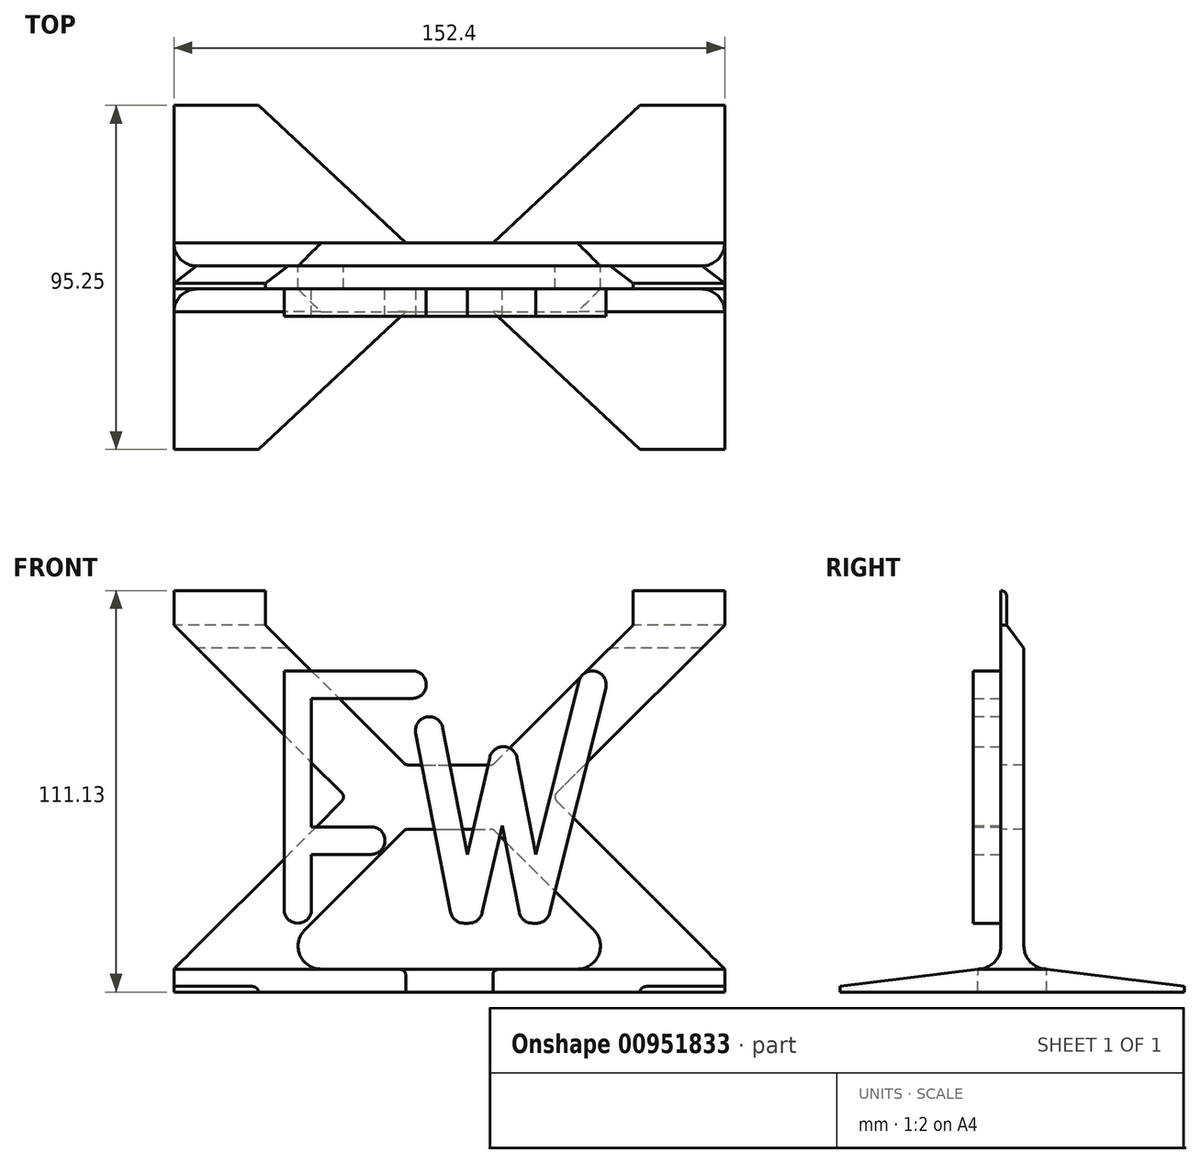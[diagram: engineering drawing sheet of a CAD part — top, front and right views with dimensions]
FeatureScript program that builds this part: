
annotation { "Feature Type Name" : "Feature", "Feature Type Description" : "" }
export const myFeature = defineFeature(function(context is Context, id is Id, definition is map)
    precondition{}
    {
        {
            var Q0;
            Q0=qCreatedBy(makeId("Right.planeOp"),FACE);
            var sketch = newSketch(context, id + "F0", { "sketchPlane" : qUnion([Q0])});
            skLineSegment(sketch, "E0", {"start": v(0, 9.53) * mm, "end": v(1.59, 9.53) * mm});
            skLineSegment(sketch, "E1", {"start": v(1.59, 9.53) * mm, "end": v(1.59, 0) * mm});
            skLineSegment(sketch, "E2", {"start": v(1.59, 0) * mm, "end": v(6.35, -6.35) * mm});
            skLineSegment(sketch, "E3", {"start": v(6.35, -6.35) * mm, "end": v(6.35, -95.25) * mm});
            skLineSegment(sketch, "E4", {"start": v(6.35, -95.25) * mm, "end": v(50.8, -95.25) * mm});
            skLineSegment(sketch, "E5", {"start": v(50.8, -95.25) * mm, "end": v(50.8, -101.6) * mm});
            skLineSegment(sketch, "E6", {"start": v(0, 9.53) * mm, "end": v(0, -95.25) * mm});
            skLineSegment(sketch, "E7", {"start": v(-44.45, -101.6) * mm, "end": v(-44.45, -95.25) * mm});
            skLineSegment(sketch, "E8", {"start": v(-44.45, -95.25) * mm, "end": v(0, -95.25) * mm});
            skLineSegment(sketch, "E9", {"start": v(-44.45, -101.6) * mm, "end": v(50.8, -101.6) * mm});
            skSolve(sketch);
        }
        {
            var Q0;
            Q0 = qSketchRegion(id + "F0", true);
            extrude(context, id + "F1", {"entities" : qUnion([Q0]), "endBound" : BoundingType.SYMMETRIC, "depth" : 152.4 * mm, "offsetDistance" : 25.4 * mm});
        }
        {
            var Q0;
            Q0=makeQuery(id+"F1.opExtrude","SWEPT_FACE",FACE,{"disambiguationData":[OSD([sQuery(id+"F0.wireOp",EDGE,"E8")])]});
            var sketch = newSketch(context, id + "F2", { "sketchPlane" : qUnion([Q0])});
            skLineSegment(sketch, "E10", {"start": v(63.5, 0) * mm, "end": v(63.5, -44.45) * mm});
            skLineSegment(sketch, "E11", {"start": v(0, -44.45) * mm, "end": v(0, 0) * mm});
            skLineSegment(sketch, "E12", {"start": v(-63.5, -44.45) * mm, "end": v(-63.5, 0) * mm});
            skLineSegment(sketch, "E13", {"start": v(-36.08, 3.18) * mm, "end": v(33.95, 3.18) * mm, "construction": true});
            skLineSegment(sketch, "E14.MirrorCS", {"start": v(-63.5, 50.8) * mm, "end": v(-63.5, 6.35) * mm});
            skLineSegment(sketch, "E15.MirrorCS", {"start": v(0, 50.8) * mm, "end": v(0, 6.35) * mm});
            skLineSegment(sketch, "E16.MirrorCS", {"start": v(63.5, 6.35) * mm, "end": v(63.5, 50.8) * mm});
            skSolve(sketch);
        }
        {
            var Q0;
            Q0=makeQuery(id+"F1.opExtrude","SWEPT_FACE",FACE,{"disambiguationData":[OSD([sQuery(id+"F0.wireOp",EDGE,"E6")])]});
            var sketch = newSketch(context, id + "F3", { "sketchPlane" : qUnion([Q0])});
            skLineSegment(sketch, "E17", {"start": v(-45.72, -12.7) * mm, "end": v(-45.72, -82.55) * mm});
            skLineSegment(sketch, "E18", {"start": v(-45.72, -82.55) * mm, "end": v(-38.1, -82.55) * mm});
            skLineSegment(sketch, "E19", {"start": v(-38.1, -82.55) * mm, "end": v(-38.1, -63.5) * mm});
            skLineSegment(sketch, "E20", {"start": v(-38.1, -63.5) * mm, "end": v(-17.78, -63.5) * mm});
            skLineSegment(sketch, "E21", {"start": v(-17.78, -63.5) * mm, "end": v(-17.78, -55.88) * mm});
            skLineSegment(sketch, "E22", {"start": v(-17.78, -55.88) * mm, "end": v(-38.1, -55.88) * mm});
            skLineSegment(sketch, "E23", {"start": v(-38.1, -55.88) * mm, "end": v(-38.1, -20.32) * mm});
            skLineSegment(sketch, "E24", {"start": v(-38.1, -20.32) * mm, "end": v(-6.35, -20.32) * mm});
            skLineSegment(sketch, "E25", {"start": v(-6.35, -20.32) * mm, "end": v(-6.35, -12.7) * mm});
            skLineSegment(sketch, "E26", {"start": v(-6.35, -12.7) * mm, "end": v(-45.72, -12.7) * mm});
            skLineSegment(sketch, "E27", {"start": v(-10.16, -25.4) * mm, "end": v(0.95, -82.55) * mm});
            skLineSegment(sketch, "E28", {"start": v(27.07, -82.55) * mm, "end": v(44.49, -12.7) * mm});
            skLineSegment(sketch, "E29", {"start": v(44.49, -12.7) * mm, "end": v(36.64, -12.7) * mm});
            skLineSegment(sketch, "E30", {"start": v(36.64, -12.7) * mm, "end": v(23.97, -63.5) * mm});
            skLineSegment(sketch, "E31", {"start": v(5, -63.5) * mm, "end": v(-2.4, -25.4) * mm});
            skLineSegment(sketch, "E32", {"start": v(-86.99, 0) * mm, "end": v(146.26, 0) * mm, "construction": true});
            skLineSegment(sketch, "E33", {"start": v(5, -63.5) * mm, "end": v(11.2, -36.7) * mm});
            skLineSegment(sketch, "E34", {"start": v(18.79, -36.83) * mm, "end": v(23.97, -63.5) * mm});
            skLineSegment(sketch, "E35", {"start": v(-10.16, -25.4) * mm, "end": v(-2.4, -25.4) * mm});
            skLineSegment(sketch, "E36", {"start": v(0.95, -82.55) * mm, "end": v(8.43, -82.55) * mm});
            skLineSegment(sketch, "E37", {"start": v(8.43, -82.55) * mm, "end": v(14.66, -55.56) * mm});
            skLineSegment(sketch, "E38", {"start": v(14.66, -55.56) * mm, "end": v(19.91, -82.55) * mm});
            skLineSegment(sketch, "E39", {"start": v(19.91, -82.55) * mm, "end": v(27.07, -82.55) * mm});
            skLineSegment(sketch, "E40", {"start": v(5, -63.5) * mm, "end": v(5, -15.04) * mm, "construction": true});
            skArc(sketch, "E41", {"start": v(18.79, -36.83) * mm, "mid": v(15.04, -33.7) * mm, "end": v(11.2, -36.7) * mm});
            skSolve(sketch);
        }
        {
            var Q0;
            Q0 = qSketchRegion(id + "F3", true);
            extrude(context, id + "F4", {"entities" : qUnion([Q0]), "depth" : 7.62 * mm, "offsetDistance" : 25.4 * mm});
        }
        {
            var Q0;
            Q0=makeQuery(id+"F4.opExtrude","SWEPT_EDGE",EDGE,{"disambiguationData":[OSD([sQuery(id+"F3.wireOp",EDGE,"E27"),sQuery(id+"F3.wireOp",EDGE,"E35")])]});
            var Q1;
            Q1=makeQuery(id+"F4.opExtrude","SWEPT_EDGE",EDGE,{"disambiguationData":[OSD([sQuery(id+"F3.wireOp",EDGE,"E31"),sQuery(id+"F3.wireOp",EDGE,"E35")])]});
            var Q2;
            Q2=makeQuery(id+"F4.opExtrude","SWEPT_EDGE",EDGE,{"disambiguationData":[OSD([sQuery(id+"F3.wireOp",EDGE,"E29"),sQuery(id+"F3.wireOp",EDGE,"E30")])]});
            var Q3;
            Q3=makeQuery(id+"F4.opExtrude","SWEPT_EDGE",EDGE,{"disambiguationData":[OSD([sQuery(id+"F3.wireOp",EDGE,"E28"),sQuery(id+"F3.wireOp",EDGE,"E29")])]});
            var Q4;
            Q4=makeQuery(id+"F4.opExtrude","SWEPT_EDGE",EDGE,{"disambiguationData":[OSD([sQuery(id+"F3.wireOp",EDGE,"E28"),sQuery(id+"F3.wireOp",EDGE,"E39")])]});
            var Q5;
            Q5=makeQuery(id+"F4.opExtrude","SWEPT_EDGE",EDGE,{"disambiguationData":[OSD([sQuery(id+"F3.wireOp",EDGE,"E36"),sQuery(id+"F3.wireOp",EDGE,"E37")])]});
            var Q6;
            Q6=makeQuery(id+"F4.opExtrude","SWEPT_EDGE",EDGE,{"disambiguationData":[OSD([sQuery(id+"F3.wireOp",EDGE,"E38"),sQuery(id+"F3.wireOp",EDGE,"E39")])]});
            var Q7;
            Q7=makeQuery(id+"F4.opExtrude","SWEPT_EDGE",EDGE,{"disambiguationData":[OSD([sQuery(id+"F3.wireOp",EDGE,"E27"),sQuery(id+"F3.wireOp",EDGE,"E36")])]});
            var Q8;
            Q8=makeQuery(id+"F4.opExtrude","SWEPT_EDGE",EDGE,{"disambiguationData":[OSD([sQuery(id+"F3.wireOp",EDGE,"E20"),sQuery(id+"F3.wireOp",EDGE,"E21")])]});
            var Q9;
            Q9=makeQuery(id+"F4.opExtrude","SWEPT_EDGE",EDGE,{"disambiguationData":[OSD([sQuery(id+"F3.wireOp",EDGE,"E21"),sQuery(id+"F3.wireOp",EDGE,"E22")])]});
            var Q10;
            Q10=makeQuery(id+"F4.opExtrude","SWEPT_EDGE",EDGE,{"disambiguationData":[OSD([sQuery(id+"F3.wireOp",EDGE,"E24"),sQuery(id+"F3.wireOp",EDGE,"E25")])]});
            var Q11;
            Q11=makeQuery(id+"F4.opExtrude","SWEPT_EDGE",EDGE,{"disambiguationData":[OSD([sQuery(id+"F3.wireOp",EDGE,"E18"),sQuery(id+"F3.wireOp",EDGE,"E19")])]});
            var Q12;
            Q12=makeQuery(id+"F4.opExtrude","SWEPT_EDGE",EDGE,{"disambiguationData":[OSD([sQuery(id+"F3.wireOp",EDGE,"E25"),sQuery(id+"F3.wireOp",EDGE,"E26")])]});
            var Q13;
            Q13=makeQuery(id+"F4.opExtrude","SWEPT_EDGE",EDGE,{"disambiguationData":[OSD([sQuery(id+"F3.wireOp",EDGE,"E17"),sQuery(id+"F3.wireOp",EDGE,"E18")])]});
            fillet(context, id + "F5", {"entities" : qUnion([Q0, Q1, Q2, Q3, Q4, Q5, Q6, Q7, Q8, Q9, Q10, Q11, Q12, Q13]), "radius" : 3.8 * mm, "tangentPropagation" : true, "allowEdgeOverflow" : false});
        }
        {
            var Q0;
            Q0=makeQuery(id+"F1.opExtrude","SWEPT_FACE",FACE,{"disambiguationData":[OSD([sQuery(id+"F0.wireOp",EDGE,"E6")])]});
            var sketch = newSketch(context, id + "F6", { "sketchPlane" : qUnion([Q0])});
            skLineSegment(sketch, "E42", {"start": v(-76.2, 0) * mm, "end": v(-28.57, -47.63) * mm});
            skLineSegment(sketch, "E43", {"start": v(-28.58, -47.63) * mm, "end": v(-76.2, -95.25) * mm});
            skLineSegment(sketch, "E44", {"start": v(-76.2, -95.25) * mm, "end": v(-76.2, 0) * mm});
            skLineSegment(sketch, "E45", {"start": v(76.2, 0) * mm, "end": v(28.57, -47.63) * mm});
            skLineSegment(sketch, "E46", {"start": v(28.57, -47.63) * mm, "end": v(76.2, -95.25) * mm});
            skLineSegment(sketch, "E47", {"start": v(76.2, -95.25) * mm, "end": v(76.2, 0) * mm});
            skLineSegment(sketch, "E48", {"start": v(-28.58, -47.63) * mm, "end": v(-76.2, -47.63) * mm, "construction": true});
            skLineSegment(sketch, "E49", {"start": v(28.58, -47.63) * mm, "end": v(76.2, -47.63) * mm, "construction": true});
            skLineSegment(sketch, "E50", {"start": v(-50.8, -95.25) * mm, "end": v(-12.06, -56.51) * mm});
            skLineSegment(sketch, "E51", {"start": v(12.06, -56.51) * mm, "end": v(50.8, -95.25) * mm});
            skLineSegment(sketch, "E52", {"start": v(-12.06, -56.52) * mm, "end": v(12.06, -56.52) * mm});
            skLineSegment(sketch, "E53.MirrorCS", {"start": v(-12.06, -38.74) * mm, "end": v(12.06, -38.74) * mm});
            skLineSegment(sketch, "E54.MirrorCS", {"start": v(-50.8, 0) * mm, "end": v(-12.06, -38.74) * mm});
            skLineSegment(sketch, "E55.MirrorCS", {"start": v(12.06, -38.74) * mm, "end": v(50.8, 0) * mm});
            skLineSegment(sketch, "E56", {"start": v(-50.8, 0) * mm, "end": v(-50.8, 9.53) * mm});
            skLineSegment(sketch, "E57", {"start": v(50.8, 0) * mm, "end": v(50.8, 9.53) * mm});
            skLineSegment(sketch, "E58", {"start": v(50.8, 9.53) * mm, "end": v(-50.8, 9.53) * mm});
            skSolve(sketch);
        }
        {
            var Q0;
            Q0=makeQuery(id+"F6.imprint","IMPRINT",FACE,{"disambiguationData":[TD([[makeQuery(id+"F6.imprint","IMPRINT",EDGE,{"derivedFrom":sQuery(id+"F6.wireOp",EDGE,"E45")}),1.0]])]});
            var Q1;
            Q1=makeQuery(id+"F6.imprint","IMPRINT",FACE,{"disambiguationData":[TD([[makeQuery(id+"F6.imprint","IMPRINT",EDGE,{"derivedFrom":sQuery(id+"F6.wireOp",EDGE,"E53.MirrorCS")}),1.0]])]});
            var Q2;
            {var subQ0=sQuery(id+"F6.wireOp",EDGE,"E50");Q2=makeQuery(id+"F6.imprint","IMPRINT",FACE,{"disambiguationData":[TD([[makeQuery(id+"F6.imprint","IMPRINT",EDGE,{"derivedFrom":subQ0}),-1.0]])]});}
            var Q3;
            Q3=makeQuery(id+"F6.imprint","IMPRINT",FACE,{"disambiguationData":[TD([[makeQuery(id+"F6.imprint","IMPRINT",EDGE,{"derivedFrom":sQuery(id+"F6.wireOp",EDGE,"E42")}),-1.0]])]});
            var Q4;
            Q4=makeQuery(id+"F6.imprint","IMPRINT",FACE,{"disambiguationData":[TD([[makeQuery(id+"F6.imprint","IMPRINT",EDGE,{"derivedFrom":sQuery(id+"F6.wireOp",EDGE,"6XojoKTg-mtFg-S1lx-smN3-pDs7Ketdyg1A")}),1.0]])]});
            extrude(context, id + "F7", {"entities" : qUnion([Q0, Q1, Q2, Q3, Q4]), "operationType" : NewBodyOperationType.REMOVE, "endBound" : BoundingType.UP_TO_NEXT, "oppositeDirection" : true, "depth" : 25.4 * mm, "offsetDistance" : 25.4 * mm});
        }
        {
            var Q0;
            {var subQ0=sQuery(id+"F0.wireOp",EDGE,"E8");var subQ1=sQuery(id+"F0.wireOp",EDGE,"E6");Q0=makeQuery(id+"F7.boolean.opBoolean","SPLIT",EDGE,{"disambiguationData":[TD([makeQuery(id+"F7.opExtrude","SWEPT_FACE",FACE,{"disambiguationData":[OSD([sQuery(id+"F6.wireOp",EDGE,"E43")])]})])],"derivedFrom":makeQuery(id+"F1.opExtrude","SWEPT_EDGE",EDGE,{"disambiguationData":[OSD([subQ1,subQ0])]})});}
            var Q1;
            {var subQ0=sQuery(id+"F0.wireOp",EDGE,"E8");var subQ1=sQuery(id+"F0.wireOp",EDGE,"E6");Q1=makeQuery(id+"F7.boolean.opBoolean","SPLIT",EDGE,{"disambiguationData":[TD([makeQuery(id+"F7.opExtrude","SWEPT_FACE",FACE,{"disambiguationData":[OSD([sQuery(id+"F6.wireOp",EDGE,"E46")])]})])],"derivedFrom":makeQuery(id+"F1.opExtrude","SWEPT_EDGE",EDGE,{"disambiguationData":[OSD([subQ1,subQ0])]})});}
            var Q2;
            {var subQ0=sQuery(id+"F0.wireOp",EDGE,"E4");var subQ2=sQuery(id+"F0.wireOp",EDGE,"E3");Q2=makeQuery(id+"F7.boolean.opBoolean","SPLIT",EDGE,{"disambiguationData":[TD([makeQuery(id+"F7.opExtrude","SWEPT_FACE",FACE,{"disambiguationData":[OSD([sQuery(id+"F6.wireOp",EDGE,"E46")])]})])],"derivedFrom":makeQuery(id+"F1.opExtrude","SWEPT_EDGE",EDGE,{"disambiguationData":[OSD([subQ2,subQ0])]})});}
            var Q3;
            {var subQ1=sQuery(id+"F0.wireOp",EDGE,"E3");var subQ2=sQuery(id+"F0.wireOp",EDGE,"E4");Q3=makeQuery(id+"F7.boolean.opBoolean","SPLIT",EDGE,{"disambiguationData":[TD([makeQuery(id+"F7.opExtrude","SWEPT_FACE",FACE,{"disambiguationData":[OSD([sQuery(id+"F6.wireOp",EDGE,"E43")])]})])],"derivedFrom":makeQuery(id+"F1.opExtrude","SWEPT_EDGE",EDGE,{"disambiguationData":[OSD([subQ1,subQ2])]})});}
            var Q4;
            Q4=makeQuery(id+"F7.boolean.opBoolean","COPY",EDGE,{"derivedFrom":makeQuery(id+"F7.opExtrude","SWEPT_EDGE",EDGE,{"disambiguationData":[OSD([sQuery(id+"F0.wireOp",EDGE,"E6"),sQuery(id+"F0.wireOp",EDGE,"E8"),sQuery(id+"F6.wireOp",EDGE,"E50")])]})});
            var Q5;
            Q5=makeQuery(id+"F7.boolean.opBoolean","COPY",EDGE,{"derivedFrom":makeQuery(id+"F7.opExtrude","SWEPT_EDGE",EDGE,{"disambiguationData":[OSD([sQuery(id+"F0.wireOp",EDGE,"E6"),sQuery(id+"F0.wireOp",EDGE,"E8"),sQuery(id+"F6.wireOp",EDGE,"E51")])]})});
            fillet(context, id + "F8", {"entities" : qUnion([Q0, Q1, Q2, Q3, Q4, Q5]), "radius" : 6.35 * mm, "tangentPropagation" : true, "allowEdgeOverflow" : false});
        }
        {
            var Q0;
            {var subQ0=sQuery(id+"F0.wireOp",EDGE,"E6");var subQ1=sQuery(id+"F0.wireOp",EDGE,"E5");var subQ2=sQuery(id+"F0.wireOp",EDGE,"E4");var subQ3=sQuery(id+"F0.wireOp",EDGE,"E3");var subQ4=sQuery(id+"F0.wireOp",EDGE,"E7");var subQ5=sQuery(id+"F0.wireOp",EDGE,"E8");var subQ6=sQuery(id+"F0.wireOp",EDGE,"E9");Q0=makeQuery(id+"F7.boolean.opBoolean","SPLIT",FACE,{"disambiguationData":[TD([makeQuery(id+"F1.opExtrude","SWEPT_FACE",FACE,{"disambiguationData":[OSD([subQ3])]})])],"derivedFrom":makeQuery(id+"F1.opExtrude","CAP_FACE",FACE,{"disambiguationData":[OSD([sQuery(id+"F0.wireOp",EDGE,"E0"),sQuery(id+"F0.wireOp",EDGE,"E1"),sQuery(id+"F0.wireOp",EDGE,"E2"),subQ3,subQ2,subQ1,subQ0,subQ4,subQ5,subQ6])],"isStart":false})});}
            var sketch = newSketch(context, id + "F9", { "sketchPlane" : qUnion([Q0])});
            skLineSegment(sketch, "E59", {"start": v(-6.35, -95.25) * mm, "end": v(-44.45, -100.01) * mm});
            skLineSegment(sketch, "E60", {"start": v(-44.45, -100.01) * mm, "end": v(-44.45, -95.25) * mm});
            skLineSegment(sketch, "E61", {"start": v(-44.45, -95.25) * mm, "end": v(-6.35, -95.25) * mm});
            skLineSegment(sketch, "E62", {"start": v(3.18, -95.25) * mm, "end": v(3.18, -76.25) * mm, "construction": true});
            skLineSegment(sketch, "E63.MirrorCS", {"start": v(12.7, -95.25) * mm, "end": v(50.8, -100.01) * mm});
            skLineSegment(sketch, "E64.MirrorCS", {"start": v(50.8, -95.25) * mm, "end": v(12.7, -95.25) * mm});
            skLineSegment(sketch, "E65.MirrorCS", {"start": v(50.8, -100.01) * mm, "end": v(50.8, -95.25) * mm});
            skSolve(sketch);
        }
        {
            var Q0;
            Q0 = qSketchRegion(id + "F9", true);
            extrude(context, id + "F10", {"entities" : qUnion([Q0]), "operationType" : NewBodyOperationType.REMOVE, "endBound" : BoundingType.THROUGH_ALL, "oppositeDirection" : true, "depth" : 25.4 * mm, "offsetDistance" : 25.4 * mm});
        }
        {
            var Q0;
            {var subQ0=sQuery(id+"F0.wireOp",EDGE,"E8");Q0=makeQuery(id+"F7.boolean.opBoolean","MERGE",FACE,{"derivedFrom":[makeQuery(id+"F1.opExtrude","SWEPT_FACE",FACE,{"disambiguationData":[OSD([sQuery(id+"F0.wireOp",EDGE,"E4")])]}),makeQuery(id+"F1.opExtrude","SWEPT_FACE",FACE,{"disambiguationData":[OSD([subQ0])]})],"fromTools":[makeQuery(id+"F7.opExtrude","SWEPT_FACE",FACE,{"disambiguationData":[OSD([sQuery(id+"F0.wireOp",EDGE,"E6"),subQ0])]})]});}
            var sketch = newSketch(context, id + "F11", { "sketchPlane" : qUnion([Q0])});
            skLineSegment(sketch, "E66", {"start": v(52.8, 50.8) * mm, "end": v(12.06, 12.7) * mm});
            skLineSegment(sketch, "E67", {"start": v(12.06, 12.7) * mm, "end": v(-12.06, 12.7) * mm});
            skLineSegment(sketch, "E68", {"start": v(-12.06, 12.7) * mm, "end": v(-52.8, 50.8) * mm});
            skLineSegment(sketch, "E69", {"start": v(-52.8, 50.8) * mm, "end": v(52.8, 50.8) * mm});
            skLineSegment(sketch, "E70.MirrorCS", {"start": v(52.8, -44.45) * mm, "end": v(12.06, -6.35) * mm});
            skLineSegment(sketch, "E71.MirrorCS", {"start": v(-52.8, -44.45) * mm, "end": v(52.8, -44.45) * mm});
            skLineSegment(sketch, "E72.MirrorCS", {"start": v(-12.06, -6.35) * mm, "end": v(-52.8, -44.45) * mm});
            skLineSegment(sketch, "E73.MirrorCS", {"start": v(12.06, -6.35) * mm, "end": v(-12.06, -6.35) * mm});
            skLineSegment(sketch, "E74", {"start": v(76.2, 50.8) * mm, "end": v(35.47, 12.7) * mm});
            skLineSegment(sketch, "E75", {"start": v(35.47, 12.7) * mm, "end": v(76.2, 12.7) * mm});
            skLineSegment(sketch, "E76", {"start": v(76.2, 12.7) * mm, "end": v(76.2, 50.8) * mm});
            skLineSegment(sketch, "E77.MirrorCS", {"start": v(-76.2, 50.8) * mm, "end": v(-35.47, 12.7) * mm});
            skLineSegment(sketch, "E78.MirrorCS", {"start": v(-35.47, 12.7) * mm, "end": v(-76.2, 12.7) * mm});
            skLineSegment(sketch, "E79.MirrorCS", {"start": v(-76.2, 12.7) * mm, "end": v(-76.2, 50.8) * mm});
            skLineSegment(sketch, "E80.MirrorCS", {"start": v(-35.47, -6.35) * mm, "end": v(-76.2, -6.35) * mm});
            skLineSegment(sketch, "E81.MirrorCS", {"start": v(-76.2, -44.45) * mm, "end": v(-35.47, -6.35) * mm});
            skLineSegment(sketch, "E82.MirrorCS", {"start": v(-76.2, -6.35) * mm, "end": v(-76.2, -44.45) * mm});
            skLineSegment(sketch, "E83.MirrorCS", {"start": v(76.2, -44.45) * mm, "end": v(35.47, -6.35) * mm});
            skLineSegment(sketch, "E84.MirrorCS", {"start": v(76.2, -6.35) * mm, "end": v(76.2, -44.45) * mm});
            skLineSegment(sketch, "E85.MirrorCS", {"start": v(35.47, -6.35) * mm, "end": v(76.2, -6.35) * mm});
            skSolve(sketch);
        }
        {
            var Q0;
            Q0=makeQuery(id+"F11.imprint","IMPRINT",FACE,{"disambiguationData":[TD([[makeQuery(id+"F11.imprint","IMPRINT",EDGE,{"derivedFrom":sQuery(id+"F11.wireOp",EDGE,"E70.MirrorCS")}),1.0]])]});
            var Q1;
            Q1=makeQuery(id+"F11.imprint","IMPRINT",FACE,{"disambiguationData":[TD([[makeQuery(id+"F11.imprint","IMPRINT",EDGE,{"derivedFrom":sQuery(id+"F11.wireOp",EDGE,"E66")}),-1.0]])]});
            extrude(context, id + "F12", {"entities" : qUnion([Q0, Q1]), "operationType" : NewBodyOperationType.REMOVE, "endBound" : BoundingType.THROUGH_ALL, "oppositeDirection" : true, "depth" : 25.4 * mm, "offsetDistance" : 25.4 * mm});
        }
        {
            var Q0;
            {var subQ0=sQuery(id+"F0.wireOp",EDGE,"E7");var subQ1=sQuery(id+"F9.wireOp",EDGE,"E59");Q0=makeQuery(id+"F12.boolean.opBoolean","SPLIT",EDGE,{"disambiguationData":[TD([makeQuery(id+"F12.opExtrude","SWEPT_FACE",FACE,{"disambiguationData":[OSD([sQuery(id+"F11.wireOp",EDGE,"E70.MirrorCS")])]})])],"derivedFrom":makeQuery(id+"F10.boolean.opBoolean","COPY",EDGE,{"derivedFrom":makeQuery(id+"F10.opExtrude","SWEPT_EDGE",EDGE,{"disambiguationData":[OSD([subQ0,subQ1,sQuery(id+"F9.wireOp",EDGE,"E60")])]})})});}
            var Q1;
            {var subQ0=sQuery(id+"F0.wireOp",EDGE,"E7");var subQ1=sQuery(id+"F9.wireOp",EDGE,"E59");Q1=makeQuery(id+"F12.boolean.opBoolean","SPLIT",EDGE,{"disambiguationData":[TD([makeQuery(id+"F12.opExtrude","SWEPT_FACE",FACE,{"disambiguationData":[OSD([sQuery(id+"F11.wireOp",EDGE,"E72.MirrorCS")])]})])],"derivedFrom":makeQuery(id+"F10.boolean.opBoolean","COPY",EDGE,{"derivedFrom":makeQuery(id+"F10.opExtrude","SWEPT_EDGE",EDGE,{"disambiguationData":[OSD([subQ0,subQ1,sQuery(id+"F9.wireOp",EDGE,"E60")])]})})});}
            var Q2;
            Q2=makeQuery(id+"F12.boolean.opBoolean","INTERSECT",EDGE,{"derivedFrom":[makeQuery(id+"F10.boolean.opBoolean","COPY",FACE,{"derivedFrom":makeQuery(id+"F10.opExtrude","SWEPT_FACE",FACE,{"disambiguationData":[OSD([sQuery(id+"F9.wireOp",EDGE,"E59")])]})}),makeQuery(id+"F12.opExtrude","SWEPT_FACE",FACE,{"disambiguationData":[OSD([sQuery(id+"F11.wireOp",EDGE,"E72.MirrorCS")])]})]});
            var Q3;
            Q3=makeQuery(id+"F12.boolean.opBoolean","INTERSECT",EDGE,{"derivedFrom":[makeQuery(id+"F10.boolean.opBoolean","COPY",FACE,{"derivedFrom":makeQuery(id+"F10.opExtrude","SWEPT_FACE",FACE,{"disambiguationData":[OSD([sQuery(id+"F9.wireOp",EDGE,"E59")])]})}),makeQuery(id+"F12.opExtrude","SWEPT_FACE",FACE,{"disambiguationData":[OSD([sQuery(id+"F11.wireOp",EDGE,"E70.MirrorCS")])]})]});
            var Q4;
            {var subQ0=sQuery(id+"F0.wireOp",EDGE,"E5");var subQ1=sQuery(id+"F9.wireOp",EDGE,"E63.MirrorCS");Q4=makeQuery(id+"F12.boolean.opBoolean","SPLIT",EDGE,{"disambiguationData":[TD([makeQuery(id+"F12.opExtrude","SWEPT_FACE",FACE,{"disambiguationData":[OSD([sQuery(id+"F11.wireOp",EDGE,"E66")])]})])],"derivedFrom":makeQuery(id+"F10.boolean.opBoolean","COPY",EDGE,{"derivedFrom":makeQuery(id+"F10.opExtrude","SWEPT_EDGE",EDGE,{"disambiguationData":[OSD([subQ0,subQ1,sQuery(id+"F9.wireOp",EDGE,"E65.MirrorCS")])]})})});}
            var Q5;
            Q5=makeQuery(id+"F12.boolean.opBoolean","INTERSECT",EDGE,{"derivedFrom":[makeQuery(id+"F10.boolean.opBoolean","COPY",FACE,{"derivedFrom":makeQuery(id+"F10.opExtrude","SWEPT_FACE",FACE,{"disambiguationData":[OSD([sQuery(id+"F9.wireOp",EDGE,"E63.MirrorCS")])]})}),makeQuery(id+"F12.opExtrude","SWEPT_FACE",FACE,{"disambiguationData":[OSD([sQuery(id+"F11.wireOp",EDGE,"E66")])]})]});
            var Q6;
            Q6=makeQuery(id+"F12.boolean.opBoolean","INTERSECT",EDGE,{"derivedFrom":[makeQuery(id+"F10.boolean.opBoolean","COPY",FACE,{"derivedFrom":makeQuery(id+"F10.opExtrude","SWEPT_FACE",FACE,{"disambiguationData":[OSD([sQuery(id+"F9.wireOp",EDGE,"E63.MirrorCS")])]})}),makeQuery(id+"F12.opExtrude","SWEPT_FACE",FACE,{"disambiguationData":[OSD([sQuery(id+"F11.wireOp",EDGE,"E68")])]})]});
            var Q7;
            {var subQ0=sQuery(id+"F0.wireOp",EDGE,"E5");var subQ1=sQuery(id+"F9.wireOp",EDGE,"E63.MirrorCS");Q7=makeQuery(id+"F12.boolean.opBoolean","SPLIT",EDGE,{"disambiguationData":[TD([makeQuery(id+"F12.opExtrude","SWEPT_FACE",FACE,{"disambiguationData":[OSD([sQuery(id+"F11.wireOp",EDGE,"E68")])]})])],"derivedFrom":makeQuery(id+"F10.boolean.opBoolean","COPY",EDGE,{"derivedFrom":makeQuery(id+"F10.opExtrude","SWEPT_EDGE",EDGE,{"disambiguationData":[OSD([subQ0,subQ1,sQuery(id+"F9.wireOp",EDGE,"E65.MirrorCS")])]})})});}
            var Q8;
            {var subQ0=sQuery(id+"F0.wireOp",EDGE,"E0");var subQ1=sQuery(id+"F0.wireOp",EDGE,"E1");Q8=makeQuery(id+"F7.boolean.opBoolean","SPLIT",EDGE,{"disambiguationData":[TD([makeQuery(id+"F7.opExtrude","SWEPT_FACE",FACE,{"disambiguationData":[OSD([sQuery(id+"F6.wireOp",EDGE,"E56")])]})])],"derivedFrom":makeQuery(id+"F1.opExtrude","SWEPT_EDGE",EDGE,{"disambiguationData":[OSD([subQ0,subQ1])]})});}
            var Q9;
            {var subQ0=sQuery(id+"F0.wireOp",EDGE,"E0");var subQ1=sQuery(id+"F0.wireOp",EDGE,"E1");Q9=makeQuery(id+"F7.boolean.opBoolean","SPLIT",EDGE,{"disambiguationData":[TD([makeQuery(id+"F7.opExtrude","SWEPT_FACE",FACE,{"disambiguationData":[OSD([sQuery(id+"F6.wireOp",EDGE,"E57")])]})])],"derivedFrom":makeQuery(id+"F1.opExtrude","SWEPT_EDGE",EDGE,{"disambiguationData":[OSD([subQ0,subQ1])]})});}
            var Q10;
            Q10=makeQuery(id+"F7.boolean.opBoolean","COPY",EDGE,{"derivedFrom":makeQuery(id+"F7.opExtrude","CAP_EDGE",EDGE,{"disambiguationData":[OSD([sQuery(id+"F6.wireOp",EDGE,"E46")])],"isStart":true})});
            var Q11;
            Q11=makeQuery(id+"F7.boolean.opBoolean","COPY",EDGE,{"derivedFrom":makeQuery(id+"F7.opExtrude","CAP_EDGE",EDGE,{"disambiguationData":[OSD([sQuery(id+"F6.wireOp",EDGE,"E45")])],"isStart":true})});
            var Q12;
            Q12=makeQuery(id+"F7.boolean.opBoolean","COPY",EDGE,{"derivedFrom":makeQuery(id+"F7.opExtrude","CAP_EDGE",EDGE,{"disambiguationData":[OSD([sQuery(id+"F6.wireOp",EDGE,"E55.MirrorCS")])],"isStart":true})});
            var Q13;
            Q13=makeQuery(id+"F7.boolean.opBoolean","COPY",EDGE,{"derivedFrom":makeQuery(id+"F7.opExtrude","CAP_EDGE",EDGE,{"disambiguationData":[OSD([sQuery(id+"F6.wireOp",EDGE,"E53.MirrorCS")])],"isStart":true})});
            var Q14;
            Q14=makeQuery(id+"F7.boolean.opBoolean","COPY",EDGE,{"derivedFrom":makeQuery(id+"F7.opExtrude","CAP_EDGE",EDGE,{"disambiguationData":[OSD([sQuery(id+"F6.wireOp",EDGE,"E54.MirrorCS")])],"isStart":true})});
            var Q15;
            Q15=makeQuery(id+"F7.boolean.opBoolean","COPY",EDGE,{"derivedFrom":makeQuery(id+"F7.opExtrude","CAP_EDGE",EDGE,{"disambiguationData":[OSD([sQuery(id+"F6.wireOp",EDGE,"E42")])],"isStart":true})});
            var Q16;
            Q16=makeQuery(id+"F7.boolean.opBoolean","COPY",EDGE,{"derivedFrom":makeQuery(id+"F7.opExtrude","CAP_EDGE",EDGE,{"disambiguationData":[OSD([sQuery(id+"F6.wireOp",EDGE,"E43")])],"isStart":true})});
            var Q17;
            Q17=makeQuery(id+"F7.boolean.opBoolean","COPY",EDGE,{"derivedFrom":makeQuery(id+"F7.opExtrude","CAP_EDGE",EDGE,{"disambiguationData":[OSD([sQuery(id+"F6.wireOp",EDGE,"E51")])],"isStart":true})});
            var Q18;
            Q18=makeQuery(id+"F7.boolean.opBoolean","COPY",EDGE,{"derivedFrom":makeQuery(id+"F7.opExtrude","CAP_EDGE",EDGE,{"disambiguationData":[OSD([sQuery(id+"F6.wireOp",EDGE,"E52")])],"isStart":true})});
            var Q19;
            Q19=makeQuery(id+"F7.boolean.opBoolean","COPY",EDGE,{"derivedFrom":makeQuery(id+"F7.opExtrude","CAP_EDGE",EDGE,{"disambiguationData":[OSD([sQuery(id+"F6.wireOp",EDGE,"E50")])],"isStart":true})});
            var Q20;
            Q20=makeQuery(id+"F7.boolean.opBoolean","COPY",EDGE,{"derivedFrom":makeQuery(id+"F7.opExtrude","SWEPT_EDGE",EDGE,{"disambiguationData":[OSD([sQuery(id+"F6.wireOp",EDGE,"E50"),sQuery(id+"F6.wireOp",EDGE,"E52")])]})});
            var Q21;
            Q21=makeQuery(id+"F7.boolean.opBoolean","COPY",EDGE,{"derivedFrom":makeQuery(id+"F7.opExtrude","SWEPT_EDGE",EDGE,{"disambiguationData":[OSD([sQuery(id+"F6.wireOp",EDGE,"E51"),sQuery(id+"F6.wireOp",EDGE,"E52")])]})});
            var Q22;
            Q22=makeQuery(id+"F7.boolean.opBoolean","COPY",EDGE,{"derivedFrom":makeQuery(id+"F7.opExtrude","SWEPT_EDGE",EDGE,{"disambiguationData":[OSD([sQuery(id+"F6.wireOp",EDGE,"E53.MirrorCS"),sQuery(id+"F6.wireOp",EDGE,"E54.MirrorCS")])]})});
            var Q23;
            Q23=makeQuery(id+"F7.boolean.opBoolean","COPY",EDGE,{"derivedFrom":makeQuery(id+"F7.opExtrude","SWEPT_EDGE",EDGE,{"disambiguationData":[OSD([sQuery(id+"F6.wireOp",EDGE,"E53.MirrorCS"),sQuery(id+"F6.wireOp",EDGE,"E55.MirrorCS")])]})});
            var Q24;
            Q24=makeQuery(id+"F7.boolean.opBoolean","COPY",EDGE,{"derivedFrom":makeQuery(id+"F7.opExtrude","SWEPT_EDGE",EDGE,{"disambiguationData":[OSD([sQuery(id+"F6.wireOp",EDGE,"E45"),sQuery(id+"F6.wireOp",EDGE,"E46")])]})});
            var Q25;
            Q25=makeQuery(id+"F7.boolean.opBoolean","COPY",EDGE,{"derivedFrom":makeQuery(id+"F7.opExtrude","SWEPT_EDGE",EDGE,{"disambiguationData":[OSD([sQuery(id+"F6.wireOp",EDGE,"E42"),sQuery(id+"F6.wireOp",EDGE,"E43")])]})});
            var Q26;
            {var subQ0=sQuery(id+"F6.wireOp",EDGE,"E45");Q26=makeQuery(id+"F7.boolean.opBoolean","COPY",EDGE,{"derivedFrom":makeQuery(id+"F7.opExtrude","CAP_EDGE",EDGE,{"disambiguationData":[OSD([subQ0]),topologyDisambiguationEdgeConnected([makeQuery(id+"F1.opExtrude","SWEPT_FACE",FACE,{"disambiguationData":[OSD([sQuery(id+"F0.wireOp",EDGE,"E3")])]})])],"isStart":false})});}
            var Q27;
            Q27=makeQuery(id+"F7.boolean.opBoolean","COPY",EDGE,{"derivedFrom":makeQuery(id+"F7.opExtrude","CAP_EDGE",EDGE,{"disambiguationData":[OSD([sQuery(id+"F6.wireOp",EDGE,"E46")])],"isStart":false})});
            var Q28;
            Q28=makeQuery(id+"F7.boolean.opBoolean","COPY",EDGE,{"derivedFrom":makeQuery(id+"F7.opExtrude","CAP_EDGE",EDGE,{"disambiguationData":[OSD([sQuery(id+"F6.wireOp",EDGE,"E51")])],"isStart":false})});
            var Q29;
            Q29=makeQuery(id+"F7.boolean.opBoolean","COPY",EDGE,{"derivedFrom":makeQuery(id+"F7.opExtrude","TWEAK_EDGE",EDGE,{"derivedFrom":[makeQuery(id+"F1.opExtrude","SWEPT_FACE",FACE,{"disambiguationData":[OSD([sQuery(id+"F0.wireOp",EDGE,"E3")])]}),makeQuery(id+"F6.imprint","IMPRINT",EDGE,{"derivedFrom":sQuery(id+"F6.wireOp",EDGE,"E43")})]})});
            var Q30;
            {var subQ0=sQuery(id+"F6.wireOp",EDGE,"E54.MirrorCS");Q30=makeQuery(id+"F7.boolean.opBoolean","COPY",EDGE,{"derivedFrom":makeQuery(id+"F7.opExtrude","CAP_EDGE",EDGE,{"disambiguationData":[OSD([subQ0]),topologyDisambiguationEdgeConnected([makeQuery(id+"F1.opExtrude","SWEPT_FACE",FACE,{"disambiguationData":[OSD([sQuery(id+"F0.wireOp",EDGE,"E3")])]})])],"isStart":false})});}
            fillet(context, id + "F13", {"entities" : qUnion([Q0, Q1, Q2, Q3, Q4, Q5, Q6, Q7, Q8, Q9, Q10, Q11, Q12, Q13, Q14, Q15, Q16, Q17, Q18, Q19, Q20, Q21, Q22, Q23, Q24, Q25, Q26, Q27, Q28, Q29, Q30]), "radius" : 1.59 * mm, "tangentPropagation" : true, "allowEdgeOverflow" : false});
        }
    });
